# Revit family: Shower-Valve_Trim-KOHLER-July-K-P16316IN
name_source: partatom
category: Specialty Equipment
units: mm (PartAtom-declared; Revit-internal decimal feet)

## family parameters
Cut with Voids When Loaded = No
Host = Face
OmniClass Number = 23.31.25.00
OmniClass Title = Toilet and Bath Specialties
Part Type = Normal
Room Calculation Point = No
Round Connector Dimension = Use Diameter
Shared = No

## types (2) — shared parameters
ADA Compliant = No
Assembly Code = C1030200
Date Modified = 05/31/2024
Default Elevation = 42"
Finish = Kohler-Metal-CP-Polished_Chrome
Handle Clearance = 3 13/16"
Height = 6 9/16"
Length = 3 3/8"
Manufacturer = Kohler Co.
Master Format 2014 = 10 28 00
Master Format 2014 Name = Toilet, Bath, and Laundry Accessories
Material = Premium Metal Construction
Product Name = July
URL = https://www.kohler.co.in
WaterSense Certified = No
Width = 4 7/16"

## per-type parameters (varying)
| type | Description | Model | Product Documentation Link | Product Page URL | Type |
| CP-Polished Chrome | Recessed bath and shower faucet trim with lever handle and diverter button in polished chrome | K-P16316IN-4FP-CP | https://techcomm.kohler.com | https://www.kohler.co.in | 1 |
| 4FS, CP-Polished Chrome | AT235 Recessed bath and shower trim | K-P16316IN-4FS-CP |  |  | 2 |

## geometry (parser evidence)
native form markers: Sweep x5
no freeform markers — native parametric forms only
